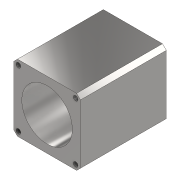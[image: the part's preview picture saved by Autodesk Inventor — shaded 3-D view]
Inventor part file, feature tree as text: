
AUTODESK INVENTOR PART (.ipt)
format: ipt  version: 2020.3 (Build 243373010, 373A)  size: 198,144 bytes
history: native  units: mm
features: sketch x4, extrude x2, hole x2, projected_geometry x2, chamfer x1
ambient origin geometry x8: Origin, YZ Plane, XZ Plane, XY Plane, X Axis, Y Axis, Z Axis, Center Point
bodies: Solid1 (feature_tree)
feature tree (11):
  extrude  "Extrusion1"  Depth=35.0mm
  chamfer  "Chamfer1"  Distance=45.0mm
  hole  "Hole1"  [1 undecoded]
  hole  "Hole2"  [1 undecoded]
  extrude  "Extrusion2"  Depth=4.242641mm
  sketch  "Sketch1"  dims[d0=35.0mm d1=35.0mm]
  sketch  "Sketch2"  dims[d2=3.0mm d3=45.0mm d4=0.0mm]
  sketch  "Sketch4"  dims[d5=2.0mm d6=2.0mm d7=45.0deg d8=3.0mm]
  projected_geometry  "Projected Loop3"
  sketch  "Sketch7"  dims[d9=4.242641mm d10=2.12132mm d11=5.0mm d12=2.5mm d13=2.5mm d14=4.242641mm d15=2.12132mm d26=5.0mm d27=2.5mm d28=5.0mm d29=2.5mm d30=2.5mm d31=2.5mm d32=2.459mm d33=6.0mm d34=4.0mm d35=2.0mm d36=90.0deg d37=8.8mm d38=20.594885mm d39=3.0mm d40=4.242641mm d41=2.12132mm d42=5.0mm d43=2.5mm d44=2.5mm d45=4.242641mm d46=2.12132mm d47=5.656854mm d48=5.0mm d49=2.5mm d50=5.0mm d51=2.5mm d52=2.5mm d53=2.5mm d54=2.459mm d55=6.0mm d56=4.0mm d57=2.0mm d58=90.0deg d59=8.8mm d60=20.594885mm d61=26.5mm d62=35.0mm d63=0.0mm d64=4.242641mm d65=0.375mm]
  projected_geometry  "Projected Loop4"
note: 2 required parameter values undecoded (feature->parameter linkage not recoverable at this tier; creation-order binding heuristic only, values carry confidence <= 0.55)
